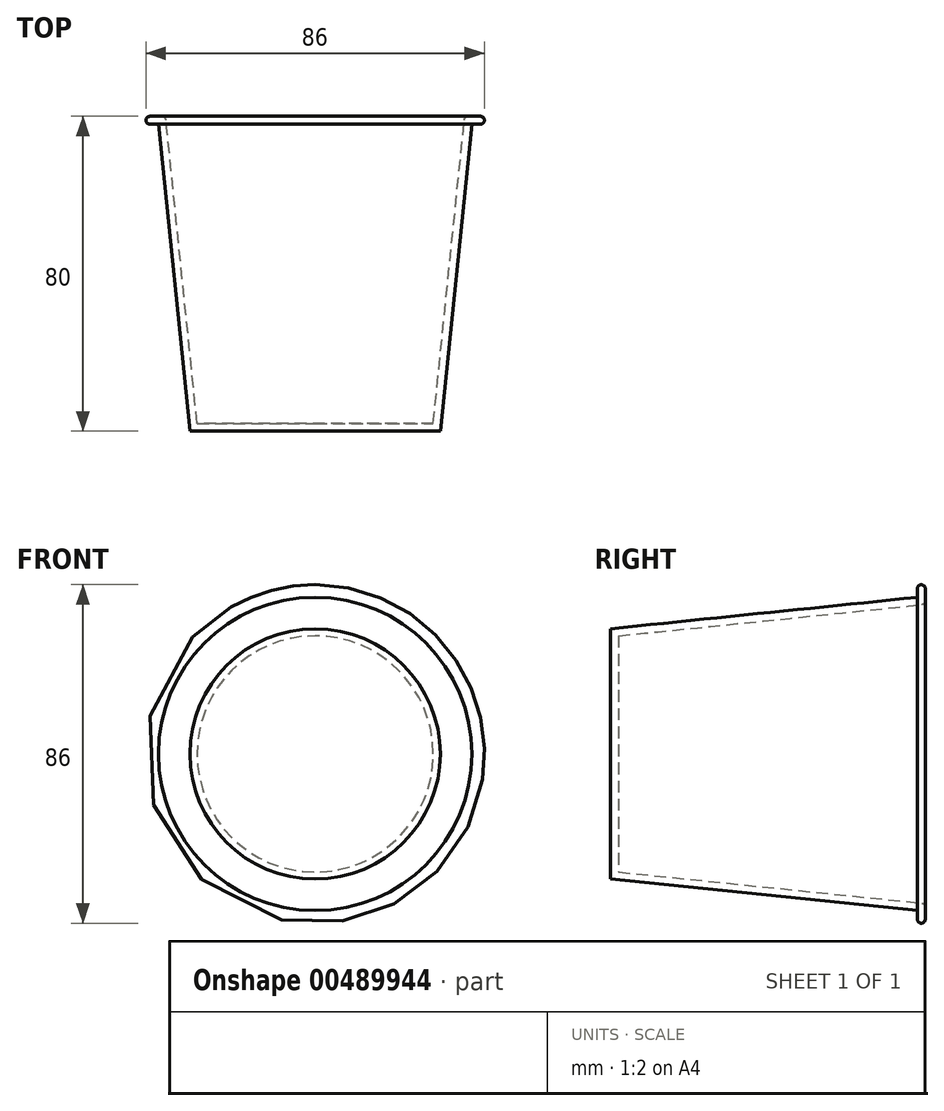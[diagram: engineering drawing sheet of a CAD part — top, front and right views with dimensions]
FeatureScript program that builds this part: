
annotation { "Feature Type Name" : "Feature", "Feature Type Description" : "" }
export const myFeature = defineFeature(function(context is Context, id is Id, definition is map)
    precondition{}
    {
        {
            var Q0;
            Q0=qCreatedBy(makeId("Top.planeOp"),FACE);
            var sketch = newSketch(context, id + "F0", { "sketchPlane" : qUnion([Q0])});
            skLineSegment(sketch, "E0", {"start": v(0, 31.85) * mm, "end": v(0, -24.56) * mm, "construction": true});
            skLineSegment(sketch, "E1", {"start": v(0, 0) * mm, "end": v(-31.8, 0) * mm});
            skLineSegment(sketch, "E2", {"start": v(-31.8, 0) * mm, "end": v(-39.8, 78) * mm});
            skLineSegment(sketch, "E3", {"start": v(0, 0) * mm, "end": v(0, 2) * mm});
            skLineSegment(sketch, "E4", {"start": v(0, 2) * mm, "end": v(-30, 2) * mm});
            skLineSegment(sketch, "E5", {"start": v(-30, 2) * mm, "end": v(-38, 80) * mm});
            skLineSegment(sketch, "E6", {"start": v(-38, 80) * mm, "end": v(-43, 80) * mm});
            skLineSegment(sketch, "E7", {"start": v(-43, 80) * mm, "end": v(-43, 78) * mm});
            skLineSegment(sketch, "E8", {"start": v(-43, 78) * mm, "end": v(-39.8, 78) * mm});
            skSolve(sketch);
        }
        {
            var Q0;
            Q0=makeQuery(id+"F0.imprint","IMPRINT",FACE,{"disambiguationData":[TD([[makeQuery(id+"F0.imprint","IMPRINT",EDGE,{"derivedFrom":sQuery(id+"F0.wireOp",EDGE,"E1")}),-1.0]])]});
            var Q1;
            Q1=sQuery(id+"F0.wireOp",EDGE,"E0");
            revolve(context, id + "F1", {"entities" : qUnion([Q0]), "axis" : qUnion([Q1]), "revolveType" : RevolveType.FULL});
        }
        {
            var Q0;
            Q0=makeQuery(id+"F1.opRevolve","SWEPT_FACE",FACE,{"disambiguationData":[OSD([sQuery(id+"F0.wireOp",EDGE,"E7")])]});
            fillet(context, id + "F2", {"entities" : qUnion([Q0]), "radius" : 1 * mm, "tangentPropagation" : true, "allowEdgeOverflow" : false});
        }
        {
            var Q0;
            Q0=makeQuery(id+"F1.opRevolve","SWEPT_EDGE",EDGE,{"disambiguationData":[OSD([sQuery(id+"F0.wireOp",EDGE,"E5"),sQuery(id+"F0.wireOp",EDGE,"E6")])]});
            fillet(context, id + "F3", {"entities" : qUnion([Q0]), "radius" : 1 * mm, "tangentPropagation" : true, "allowEdgeOverflow" : false});
        }
    });
